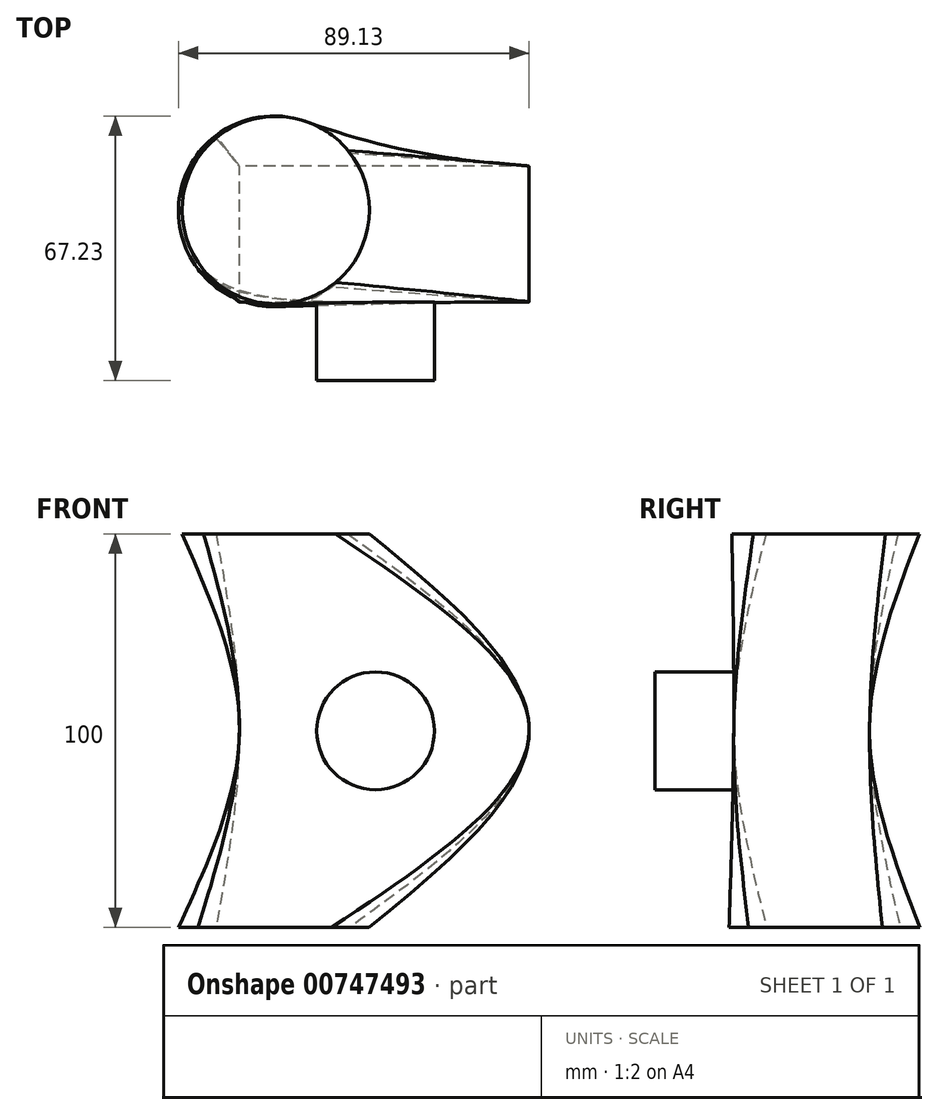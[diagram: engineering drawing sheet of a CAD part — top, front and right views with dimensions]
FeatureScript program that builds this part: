
annotation { "Feature Type Name" : "Feature", "Feature Type Description" : "" }
export const myFeature = defineFeature(function(context is Context, id is Id, definition is map)
    precondition{}
    {
        {
            var Q0;
            Q0=qCreatedBy(makeId("Top.planeOp"),FACE);
            var sketch = newSketch(context, id + "F0", { "sketchPlane" : qUnion([Q0])});
            skLineSegment(sketch, "E0.bottom", {"start": v(-34.6, 14.46) * mm, "end": v(39.04, 14.46) * mm});
            skLineSegment(sketch, "E0.top", {"start": v(-34.6, -20.05) * mm, "end": v(39.04, -20.05) * mm});
            skLineSegment(sketch, "E0.left", {"start": v(-34.6, 14.46) * mm, "end": v(-34.6, -20.05) * mm});
            skLineSegment(sketch, "E0.right", {"start": v(39.04, 14.46) * mm, "end": v(39.04, -20.05) * mm});
            skSolve(sketch);
        }
        {
            var Q0;
            Q0=qCreatedBy(makeId("Top.planeOp"),FACE);
            cPlane(context, id + "F1", {"entities" : qUnion([Q0]), "cplaneType" : CPlaneType.OFFSET, "offset" : 50 * mm, "width" : 150 * mm, "height" : 150 * mm});
        }
        {
            var Q0;
            Q0=qCreatedBy(id+"F1.planeOp",FACE);
            var sketch = newSketch(context, id + "F2", { "sketchPlane" : qUnion([Q0])});
            skCircle(sketch, "E1", {"center": v(-25.35, 3.28) * mm, "radius": 23.8 * mm});
            skSolve(sketch);
        }
        {
            var Q0;
            Q0=qCreatedBy(makeId("Top.planeOp"),FACE);
            cPlane(context, id + "F3", {"entities" : qUnion([Q0]), "cplaneType" : CPlaneType.OFFSET, "offset" : 50 * mm, "oppositeDirection" : true, "width" : 150 * mm, "height" : 150 * mm});
        }
        {
            var Q0;
            Q0=qCreatedBy(id+"F3.planeOp",FACE);
            var sketch = newSketch(context, id + "F4", { "sketchPlane" : qUnion([Q0])});
            skCircle(sketch, "E2", {"center": v(-25.86, 3) * mm, "radius": 24.23 * mm});
            skSolve(sketch);
        }
        {
            var Q0;
            Q0=makeQuery(id+"F2.imprint","IMPRINT",FACE,{"disambiguationData":[TD([[makeQuery(id+"F2.imprint","IMPRINT",EDGE,{"derivedFrom":sQuery(id+"F2.wireOp",EDGE,"E1")}),1.0]])]});
            var Q1;
            Q1=makeQuery(id+"F0.imprint","IMPRINT",FACE,{"disambiguationData":[TD([[makeQuery(id+"F0.imprint","IMPRINT",EDGE,{"derivedFrom":sQuery(id+"F0.wireOp",EDGE,"E0.bottom")}),-1.0]])]});
            var Q2;
            Q2=makeQuery(id+"F4.imprint","IMPRINT",FACE,{"disambiguationData":[TD([[makeQuery(id+"F4.imprint","IMPRINT",EDGE,{"derivedFrom":sQuery(id+"F4.wireOp",EDGE,"E2")}),1.0]])]});
            loft(context, id + "F5", {"sheetProfilesArray" : [{ "sheetProfileEntities" : qUnion([Q0]) }, { "sheetProfileEntities" : qUnion([Q1]) }, { "sheetProfileEntities" : qUnion([Q2]) }]});
        }
        {
            var Q0;
            Q0=qCreatedBy(makeId("Front.planeOp"),FACE);
            var sketch = newSketch(context, id + "F6", { "sketchPlane" : qUnion([Q0])});
            skCircle(sketch, "E3", {"center": v(0, 0) * mm, "radius": 14.96 * mm});
            skSolve(sketch);
        }
        {
            var Q0;
            Q0 = qSketchRegion(id + "F6", true);
            extrude(context, id + "F7", {"entities" : qUnion([Q0]), "operationType" : NewBodyOperationType.ADD, "depth" : 40 * mm, "offsetDistance" : 25 * mm});
        }
    });
